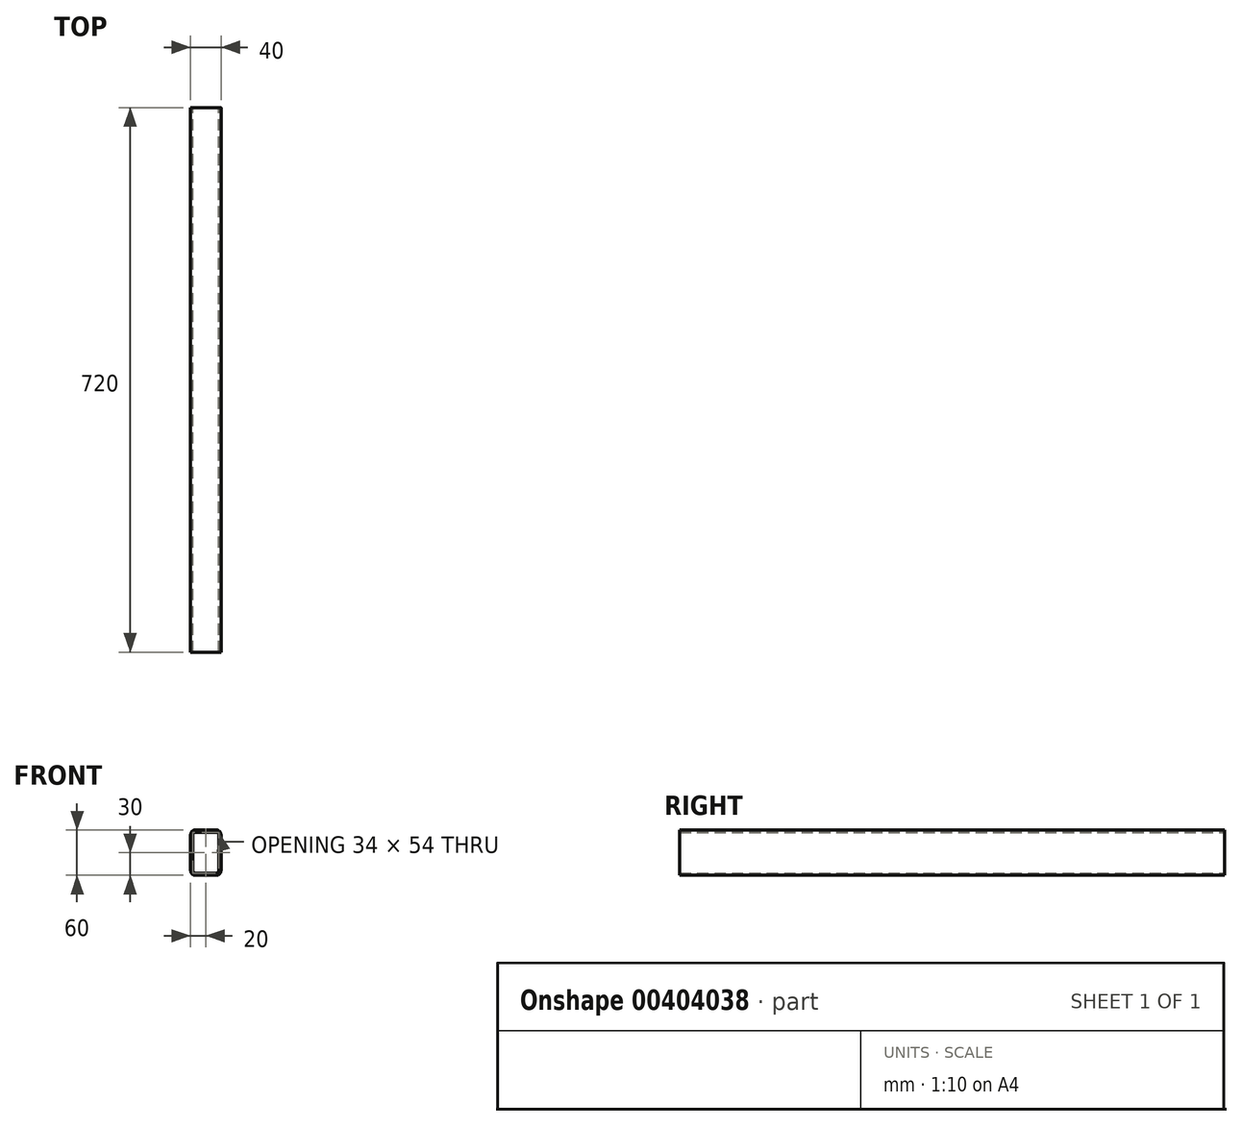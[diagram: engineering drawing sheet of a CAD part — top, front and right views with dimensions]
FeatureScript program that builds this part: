
annotation { "Feature Type Name" : "Feature", "Feature Type Description" : "" }
export const myFeature = defineFeature(function(context is Context, id is Id, definition is map)
    precondition{}
    {
        {
            var Q0;
            Q0=qCreatedBy(makeId("Front.planeOp"),FACE);
            var sketch = newSketch(context, id + "F0", { "sketchPlane" : qUnion([Q0])});
            skLineSegment(sketch, "E0.bottom", {"start": v(-14, 30) * mm, "end": v(14, 30) * mm});
            skLineSegment(sketch, "E0.top", {"start": v(-14, -30) * mm, "end": v(14, -30) * mm});
            skLineSegment(sketch, "E0.left", {"start": v(-20, 24) * mm, "end": v(-20, -24) * mm});
            skLineSegment(sketch, "E0.right", {"start": v(20, 24) * mm, "end": v(20, -24) * mm});
            skPoint(sketch, "E1.visualSharp", {"position": v(-20, 30) * mm});
            skArc(sketch, "E1.filletArc", {"start": v(-14, 30) * mm, "mid": v(-18.24, 28.24) * mm, "end": v(-20, 24) * mm});
            skPoint(sketch, "E2.visualSharp", {"position": v(-20, -30) * mm});
            skArc(sketch, "E2.filletArc", {"start": v(-20, -24) * mm, "mid": v(-18.24, -28.24) * mm, "end": v(-14, -30) * mm});
            skPoint(sketch, "E3.visualSharp", {"position": v(20, -30) * mm});
            skArc(sketch, "E3.filletArc", {"start": v(14, -30) * mm, "mid": v(18.24, -28.24) * mm, "end": v(20, -24) * mm});
            skPoint(sketch, "E4.visualSharp", {"position": v(20, 30) * mm});
            skArc(sketch, "E4.filletArc", {"start": v(20, 24) * mm, "mid": v(18.24, 28.24) * mm, "end": v(14, 30) * mm});
            skLineSegment(sketch, "E5.0", {"start": v(-17, 24) * mm, "end": v(-17, -24) * mm});
            skLineSegment(sketch, "E6.0", {"start": v(-14, 27) * mm, "end": v(14, 27) * mm});
            skArc(sketch, "E6.1", {"start": v(17, 24) * mm, "mid": v(16.12, 26.12) * mm, "end": v(14, 27) * mm});
            skLineSegment(sketch, "E6.2", {"start": v(17, 24) * mm, "end": v(17, -24) * mm});
            skArc(sketch, "E6.4", {"start": v(-17, -24) * mm, "mid": v(-16.12, -26.12) * mm, "end": v(-14, -27) * mm});
            skLineSegment(sketch, "E6.5", {"start": v(-14, -27) * mm, "end": v(14, -27) * mm});
            skArc(sketch, "E6.6", {"start": v(14, -27) * mm, "mid": v(16.12, -26.12) * mm, "end": v(17, -24) * mm});
            skArc(sketch, "E7.0", {"start": v(-14, 27) * mm, "mid": v(-16.12, 26.12) * mm, "end": v(-17, 24) * mm});
            skSolve(sketch);
        }
        {
            var Q0;
            Q0=makeQuery(id+"F0.imprint","IMPRINT",FACE,{"disambiguationData":[TD([[makeQuery(id+"F0.imprint","IMPRINT",EDGE,{"derivedFrom":sQuery(id+"F0.wireOp",EDGE,"E0.bottom")}),-1.0]])]});
            extrude(context, id + "F1", {"entities" : qUnion([Q0]), "depth" : 720 * mm});
        }
    });
